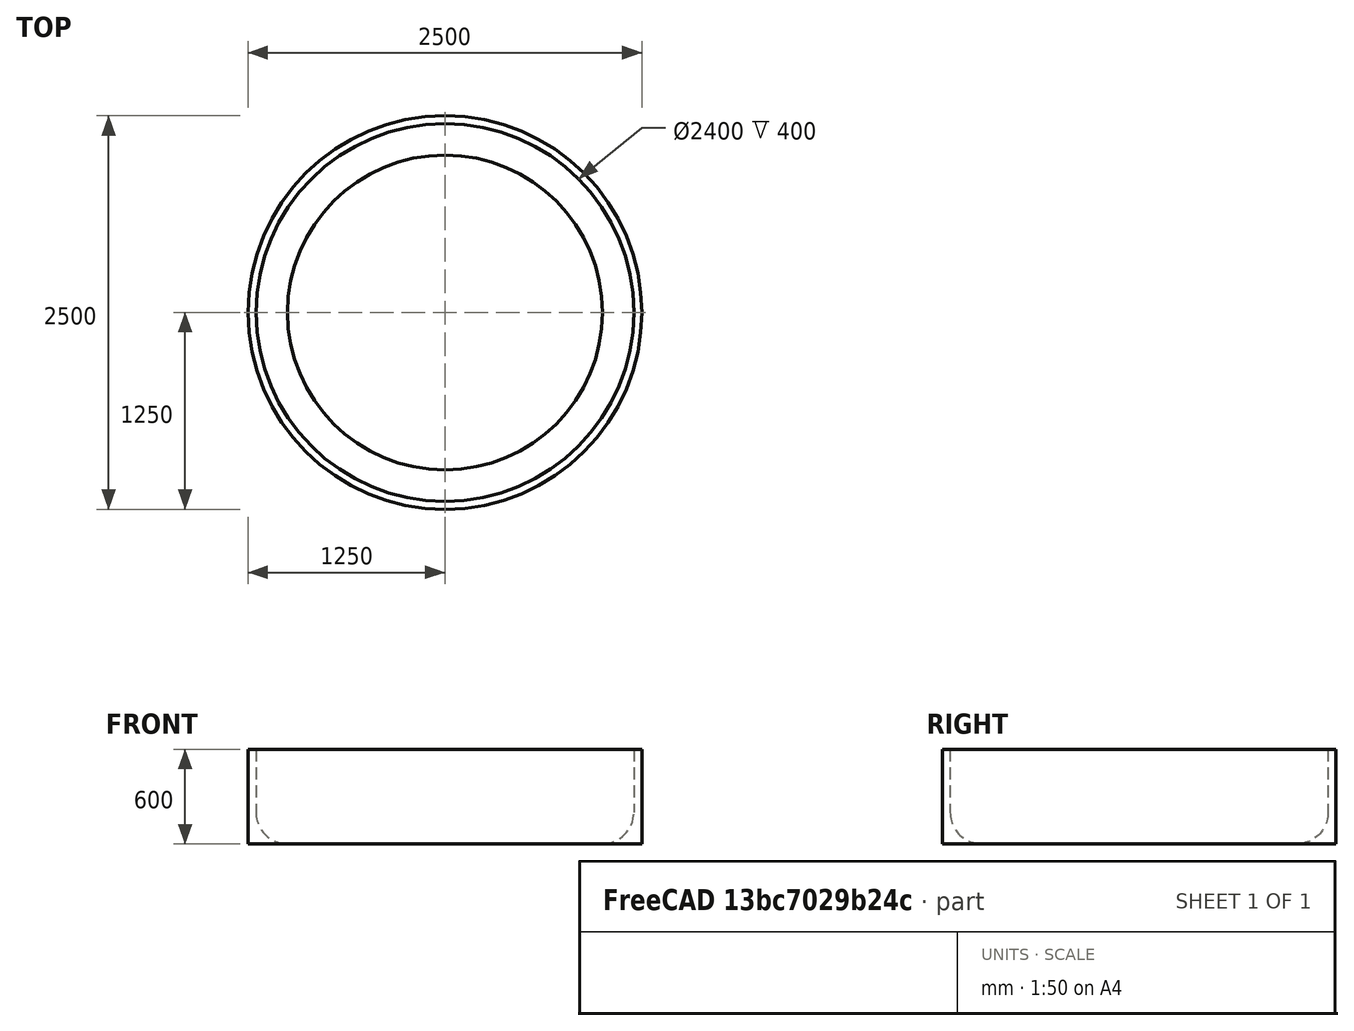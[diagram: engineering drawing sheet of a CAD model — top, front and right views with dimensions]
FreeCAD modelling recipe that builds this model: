
FCSTD DOCUMENT  (FreeCAD 0.15R4671 (Git))
Label: arena
License: All rights reserved
LicenseURL: http://en.wikipedia.org/wiki/All_rights_reserved
objects: Sketcher::SketchObject×1, Part::Revolution×1
note: 2 computed .brp shape members not serialized (recipe doc carries the construction recipe); baked Part::Feature solids carry a one-line shape summary decoded from their .brp

FEATURE [Sketcher::SketchObject] Sketch002
  Placement = pos=(0,0,0) rot=(-1,0,0;4.71239rad)
  sketch-geometry (5):
    g0: LineSegment StartX=1250 StartY=1.1e-11 StartZ=0 EndX=1250 EndY=600 EndZ=0
    g1: LineSegment StartX=1250 StartY=1.1e-11 StartZ=0 EndX=1000 EndY=1.1e-11 EndZ=0
    g2: LineSegment StartX=1250 StartY=600 StartZ=0 EndX=1200 EndY=600 EndZ=0
    g3: LineSegment StartX=1200 StartY=600 StartZ=0 EndX=1200 EndY=200 EndZ=0
    g4: ArcOfCircle CenterX=1000 CenterY=200 CenterZ=0 NormalX=0 NormalY=0 NormalZ=1 Radius=200 StartAngle=4.71239 EndAngle=6.28319
  constraints (16):
    c: Vertical(g0)
    c: Coincident(g1,g0)
    c: Horizontal(g1)
    c: DistanceX(g-1,g1) = 1000
    c: DistanceX(g-1,g0) = 1250
    c: DistanceY(g-1,g1) = 0
    c: DistanceY(g-1,g0) = 600
    c: Coincident(g2,g0)
    c: Horizontal(g2)
    c: DistanceX(g-1,g2) = 1200
    c: Coincident(g3,g2)
    c: Vertical(g3)
    c: DistanceY(g3) = -400
    c: Coincident(g4,g1)
    c: Coincident(g4,g3)
    c: Radius(g4) = 200
FEATURE [Part::Revolution] Revolve
  Angle = 360
  Axis = (0,0,1)
  Base = (0,0,0)
  Solid = false
  Source = -> Sketch002
